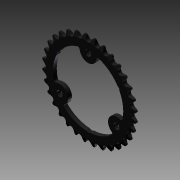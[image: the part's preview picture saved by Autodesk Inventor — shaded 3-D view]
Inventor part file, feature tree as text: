
AUTODESK INVENTOR PART (.ipt)
format: ipt  version: 2012 (Build 160160000, 160)  size: 841,216 bytes
history: native  units: in
note: dims shown in document units (in); Inventor stores cm internally (conversion verified against a paired STEP export)
features: boolean_combine x1, extrude x1, imported_body x1, sketch x1
ambient origin geometry x8: Origin, YZ Plane, XZ Plane, XY Plane, X Axis, Y Axis, Z Axis, Center Point
feature tree (4):
  boolean_combine  "Combine1"
  extrude  "Extrusion1"  [1 undecoded]
  imported_body  "Base1"
  sketch  "Sketch1"  dims[d0=1.0in d1=0.0in]
note: 1 required parameter value undecoded (feature->parameter linkage not recoverable at this tier; creation-order binding heuristic only, values carry confidence <= 0.55)
